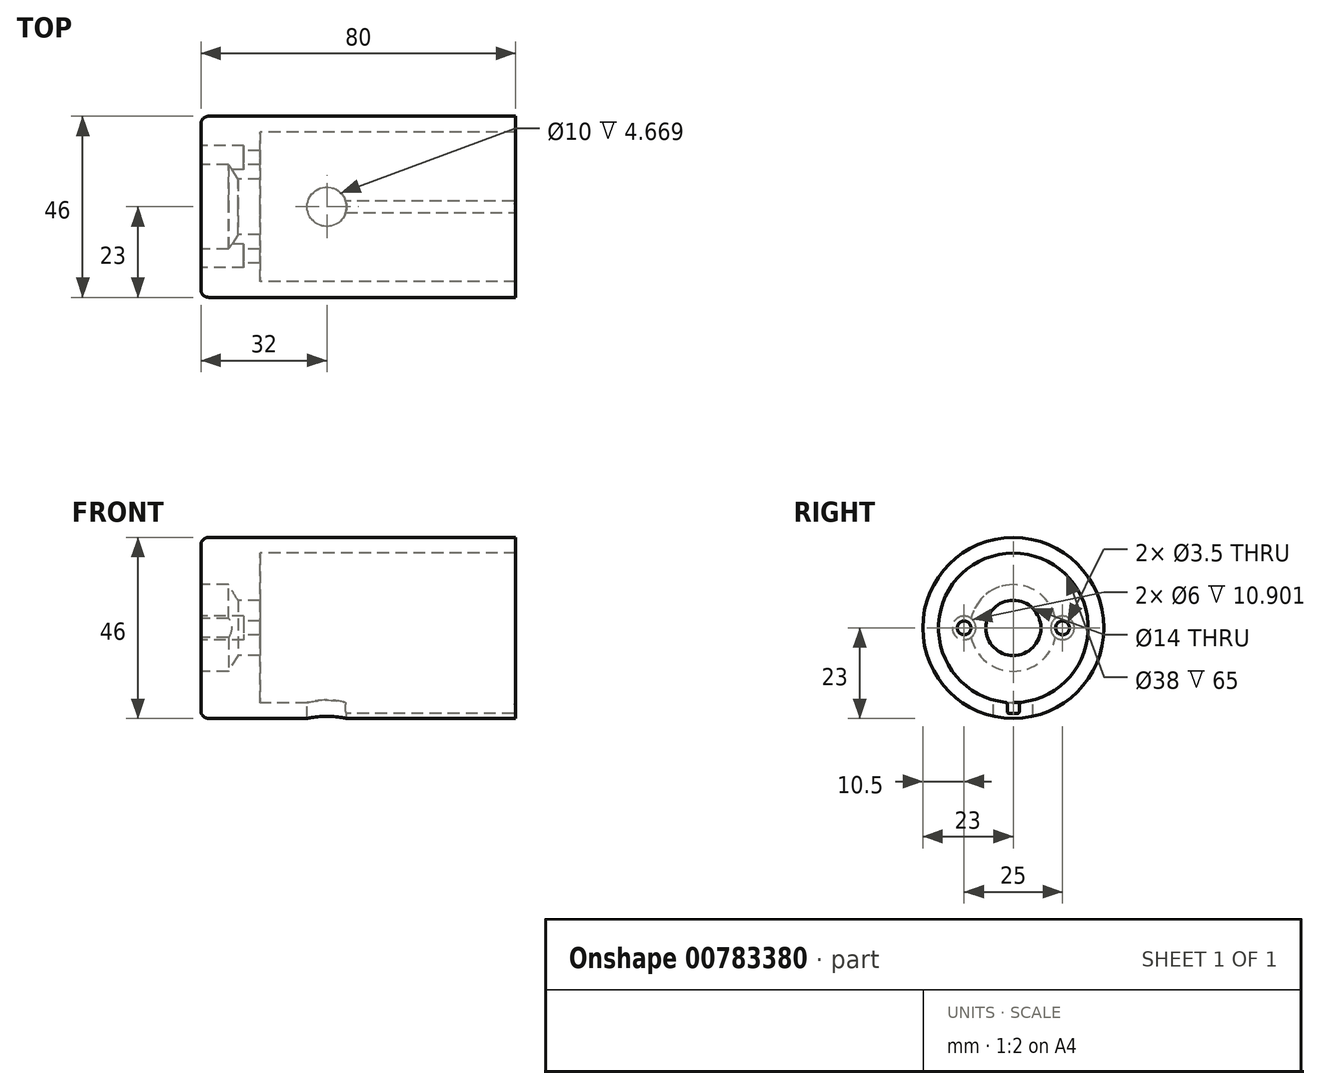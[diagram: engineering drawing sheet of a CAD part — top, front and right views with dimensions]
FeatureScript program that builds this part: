
annotation { "Feature Type Name" : "Feature", "Feature Type Description" : "" }
export const myFeature = defineFeature(function(context is Context, id is Id, definition is map)
    precondition{}
    {
        {
            var Q0;
            Q0=qCreatedBy(makeId("Right.planeOp"),FACE);
            var sketch = newSketch(context, id + "F0", { "sketchPlane" : qUnion([Q0])});
            skCircle(sketch, "E0", {"center": v(0, 0) * mm, "radius": 23 * mm});
            skCircle(sketch, "E1", {"center": v(0, 0) * mm, "radius": 19 * mm});
            skPoint(sketch, "E2", {"position": v(0, -23) * mm});
            skLineSegment(sketch, "E3", {"start": v(0, -23) * mm, "end": v(0, -18.78) * mm});
            skLineSegment(sketch, "E4", {"start": v(0, -18.78) * mm, "end": v(1.5, -18.78) * mm});
            skLineSegment(sketch, "E5", {"start": v(1.5, -18.78) * mm, "end": v(1.5, -21.78) * mm});
            skLineSegment(sketch, "E6", {"start": v(1.5, -21.78) * mm, "end": v(-1.5, -21.78) * mm});
            skLineSegment(sketch, "E7", {"start": v(-1.5, -21.78) * mm, "end": v(-1.5, -18.78) * mm});
            skLineSegment(sketch, "E8", {"start": v(-1.5, -18.78) * mm, "end": v(0, -18.78) * mm});
            skLineSegment(sketch, "E9", {"start": v(0, 0) * mm, "end": v(12.5, 0) * mm});
            skLineSegment(sketch, "E10", {"start": v(0, 0) * mm, "end": v(-12.5, 0) * mm});
            skSolve(sketch);
        }
        {
            var Q0;
            Q0=makeQuery(id+"F0.imprint","IMPRINT",FACE,{"disambiguationData":[TD([[makeQuery(id+"F0.imprint","IMPRINT",EDGE,{"derivedFrom":sQuery(id+"F0.wireOp",EDGE,"E0")}),1.0]])]});
            extrude(context, id + "F1", {"entities" : qUnion([Q0]), "depth" : 80 * mm, "offsetDistance" : 25 * mm});
        }
        {
            var Q0;
            Q0 = qSketchRegion(id + "F0", true);
            var Q1;
            {var subQ1=sQuery(id+"F0.wireOp",EDGE,"E4");Q1=makeQuery(id+"F0.imprint","IMPRINT",FACE,{"disambiguationData":[TD([[makeQuery(id+"F0.imprint","IMPRINT",EDGE,{"derivedFrom":subQ1}),1.0]])]});}
            var Q2;
            {var subQ0=sQuery(id+"F0.wireOp",EDGE,"E3");Q2=makeQuery(id+"F0.imprint","IMPRINT",FACE,{"disambiguationData":[TD([[makeQuery(id+"F0.imprint","IMPRINT",EDGE,{"derivedFrom":subQ0}),1.0]])]});}
            var Q3;
            {var subQ0=sQuery(id+"F0.wireOp",EDGE,"E3");Q3=makeQuery(id+"F0.imprint","IMPRINT",FACE,{"disambiguationData":[TD([[makeQuery(id+"F0.imprint","IMPRINT",EDGE,{"derivedFrom":subQ0}),-1.0]])]});}
            extrude(context, id + "F2", {"entities" : qUnion([Q0, Q1, Q2, Q3]), "operationType" : NewBodyOperationType.ADD, "depth" : 15 * mm, "offsetDistance" : 25 * mm});
        }
        {
            var Q0;
            Q0=qCreatedBy(makeId("Top.planeOp"),FACE);
            var sketch = newSketch(context, id + "F3", { "sketchPlane" : qUnion([Q0])});
            skLineSegment(sketch, "E11", {"start": v(0, 0) * mm, "end": v(32, 0) * mm});
            skSolve(sketch);
        }
        {
            var Q0;
            {var subQ0=sQuery(id+"F0.wireOp",EDGE,"E6");Q0=makeQuery(id+"F0.imprint","IMPRINT",FACE,{"disambiguationData":[TD([[makeQuery(id+"F0.imprint","IMPRINT",EDGE,{"derivedFrom":subQ0}),-1.0]])]});}
            extrude(context, id + "F4", {"entities" : qUnion([Q0]), "operationType" : NewBodyOperationType.ADD, "depth" : 28 * mm, "offsetDistance" : 25 * mm});
        }
        {
            var Q0;
            Q0=sQuery(id+"F3.wireOp",VERTEX,"E11.end");
            var Q1;
            Q1=makeQuery(id+"F1.opExtrude","SWEPT_BODY",BODY,{"disambiguationData":[OSD([sQuery(id+"F0.wireOp",EDGE,"E0"),sQuery(id+"F0.wireOp",EDGE,"E1"),sQuery(id+"F0.wireOp",EDGE,"E5"),sQuery(id+"F0.wireOp",EDGE,"E6"),sQuery(id+"F0.wireOp",EDGE,"E7")])]});
            hole(context, id + "F5", {"style" : HoleStyle.SIMPLE, "endStyle" : HoleEndStyle.THROUGH, "holeDiameter" : 10 * mm, "majorDiameter" : 5 * mm, "isTappedThrough" : true, "tappedDepth" : 12 * mm, "tapClearance" : 3, "locations" : qUnion([Q0]), "scope" : qUnion([Q1])});
        }
        {
            var Q0;
            Q0=sQuery(id+"F0.wireOp",VERTEX,"E0.center");
            var Q1;
            Q1=makeQuery(id+"F1.opExtrude","SWEPT_BODY",BODY,{"disambiguationData":[OSD([sQuery(id+"F0.wireOp",EDGE,"E0"),sQuery(id+"F0.wireOp",EDGE,"E1"),sQuery(id+"F0.wireOp",EDGE,"E5"),sQuery(id+"F0.wireOp",EDGE,"E6"),sQuery(id+"F0.wireOp",EDGE,"E7")])]});
            hole(context, id + "F6", {"style" : HoleStyle.SIMPLE, "endStyle" : HoleEndStyle.THROUGH, "oppositeDirection" : true, "holeDiameter" : 14 * mm, "majorDiameter" : 5 * mm, "isTappedThrough" : true, "tappedDepth" : 12 * mm, "tapClearance" : 3, "locations" : qUnion([Q0]), "scope" : qUnion([Q1])});
        }
        {
            var Q0;
            Q0=sQuery(id+"F0.wireOp",VERTEX,"E0.center");
            var Q1;
            Q1=makeQuery(id+"F1.opExtrude","SWEPT_BODY",BODY,{"disambiguationData":[OSD([sQuery(id+"F0.wireOp",EDGE,"E0"),sQuery(id+"F0.wireOp",EDGE,"E1"),sQuery(id+"F0.wireOp",EDGE,"E5"),sQuery(id+"F0.wireOp",EDGE,"E6"),sQuery(id+"F0.wireOp",EDGE,"E7")])]});
            hole(context, id + "F7", {"style" : HoleStyle.SIMPLE, "endStyle" : HoleEndStyle.BLIND, "oppositeDirection" : true, "holeDiameter" : 22 * mm, "majorDiameter" : 5 * mm, "holeDepth" : 7 * mm, "isTappedThrough" : true, "tappedDepth" : 12 * mm, "tapClearance" : 3, "locations" : qUnion([Q0]), "scope" : qUnion([Q1])});
        }
        {
            var Q0;
            Q0=sQuery(id+"F0.wireOp",VERTEX,"E9.end");
            var Q1;
            Q1=sQuery(id+"F0.wireOp",VERTEX,"E10.end");
            var Q2;
            Q2=makeQuery(id+"F1.opExtrude","SWEPT_BODY",BODY,{"disambiguationData":[OSD([sQuery(id+"F0.wireOp",EDGE,"E0"),sQuery(id+"F0.wireOp",EDGE,"E1"),sQuery(id+"F0.wireOp",EDGE,"E5"),sQuery(id+"F0.wireOp",EDGE,"E6"),sQuery(id+"F0.wireOp",EDGE,"E7")])]});
            hole(context, id + "F8", {"style" : HoleStyle.C_BORE, "endStyle" : HoleEndStyle.THROUGH, "oppositeDirection" : true, "holeDiameter" : 3.5 * mm, "cBoreDiameter" : 6 * mm, "cBoreDepth" : 3 * mm, "majorDiameter" : 5 * mm, "isTappedThrough" : true, "tappedDepth" : 12 * mm, "tapClearance" : 3, "locations" : qUnion([Q0, Q1]), "scope" : qUnion([Q2])});
        }
        {
            var Q0;
            Q0=makeQuery(id+"F2.boolean.opBoolean","SPLIT",EDGE,{"derivedFrom":makeQuery(id+"F1.opExtrude","SWEPT_EDGE",EDGE,{"disambiguationData":[OSD([sQuery(id+"F0.wireOp",EDGE,"E0"),sQuery(id+"F0.wireOp",EDGE,"E5")])]})});
            var Q1;
            Q1=makeQuery(id+"F2.boolean.opBoolean","SPLIT",EDGE,{"derivedFrom":makeQuery(id+"F1.opExtrude","SWEPT_EDGE",EDGE,{"disambiguationData":[OSD([sQuery(id+"F0.wireOp",EDGE,"E0"),sQuery(id+"F0.wireOp",EDGE,"E7")])]})});
            var Q2;
            Q2=makeQuery(id+"F1.opExtrude","CAP_EDGE",EDGE,{"disambiguationData":[OSD([sQuery(id+"F0.wireOp",EDGE,"E5")])],"isStart":false});
            var Q3;
            Q3=makeQuery(id+"F1.opExtrude","CAP_EDGE",EDGE,{"disambiguationData":[OSD([sQuery(id+"F0.wireOp",EDGE,"E7")])],"isStart":false});
            var Q4;
            Q4=makeQuery(id+"F7.hole-0.boolean.opBoolean","COPY",EDGE,{"derivedFrom":makeQuery(id+"F7.hole-0.opRevolve","SWEPT_EDGE",EDGE,{"disambiguationData":[OSD([sQuery(id+"F7.hole-0.sketch.wireOp",EDGE,"core_line_2"),sQuery(id+"F7.hole-0.sketch.wireOp",EDGE,"core_line_3")])]})});
            var Q5;
            Q5=makeQuery(id+"F7.hole-0.boolean.opBoolean","INTERSECT",EDGE,{"derivedFrom":[makeQuery(id+"F6.hole-0.boolean.opBoolean","COPY",FACE,{"derivedFrom":makeQuery(id+"F6.hole-0.opRevolve","SWEPT_FACE",FACE,{"disambiguationData":[OSD([sQuery(id+"F6.hole-0.sketch.wireOp",EDGE,"core_line_2")])]})}),makeQuery(id+"F7.hole-0.opRevolve","SWEPT_FACE",FACE,{"disambiguationData":[OSD([sQuery(id+"F7.hole-0.sketch.wireOp",EDGE,"core_line_1")])]})]});
            var Q6;
            Q6=makeQuery(id+"F6.hole-0.boolean.opBoolean","INTERSECT",EDGE,{"derivedFrom":[makeQuery(id+"F2.opExtrude","CAP_FACE",FACE,{"disambiguationData":[OSD([sQuery(id+"F0.wireOp",EDGE,"E0"),sQuery(id+"F0.wireOp",EDGE,"E1"),sQuery(id+"F0.wireOp",EDGE,"E5"),sQuery(id+"F0.wireOp",EDGE,"E6"),sQuery(id+"F0.wireOp",EDGE,"E7")])],"isStart":false}),makeQuery(id+"F6.hole-0.opRevolve","SWEPT_FACE",FACE,{"disambiguationData":[OSD([sQuery(id+"F6.hole-0.sketch.wireOp",EDGE,"core_line_2")])]})]});
            var Q7;
            Q7=makeQuery(id+"F8.hole-0.boolean.opBoolean","COPY",EDGE,{"derivedFrom":makeQuery(id+"F8.hole-0.opRevolve","SWEPT_EDGE",EDGE,{"disambiguationData":[OSD([sQuery(id+"F8.hole-0.sketch.wireOp",EDGE,"cbore_start_line_2"),sQuery(id+"F8.hole-0.sketch.wireOp",EDGE,"cbore_start_line_3")])]})});
            var Q8;
            Q8=makeQuery(id+"F8.hole-1.boolean.opBoolean","COPY",EDGE,{"derivedFrom":makeQuery(id+"F8.hole-1.opRevolve","SWEPT_EDGE",EDGE,{"disambiguationData":[OSD([sQuery(id+"F8.hole-1.sketch.wireOp",EDGE,"cbore_start_line_2"),sQuery(id+"F8.hole-1.sketch.wireOp",EDGE,"cbore_start_line_3")])]})});
            var Q9;
            Q9=makeQuery(id+"F8.hole-0.boolean.opBoolean","INTERSECT",EDGE,{"disambiguationData":[OD(1.0)],"derivedFrom":[makeQuery(id+"F7.hole-0.boolean.opBoolean","COPY",FACE,{"derivedFrom":makeQuery(id+"F7.hole-0.opRevolve","SWEPT_FACE",FACE,{"disambiguationData":[OSD([sQuery(id+"F7.hole-0.sketch.wireOp",EDGE,"core_line_2")])]})}),makeQuery(id+"F8.hole-0.opRevolve","SWEPT_FACE",FACE,{"disambiguationData":[OSD([sQuery(id+"F8.hole-0.sketch.wireOp",EDGE,"cbore_start_line_2")])]})]});
            var Q10;
            Q10=makeQuery(id+"F8.hole-0.boolean.opBoolean","INTERSECT",EDGE,{"disambiguationData":[OD(0.0)],"derivedFrom":[makeQuery(id+"F7.hole-0.boolean.opBoolean","COPY",FACE,{"derivedFrom":makeQuery(id+"F7.hole-0.opRevolve","SWEPT_FACE",FACE,{"disambiguationData":[OSD([sQuery(id+"F7.hole-0.sketch.wireOp",EDGE,"core_line_2")])]})}),makeQuery(id+"F8.hole-0.opRevolve","SWEPT_FACE",FACE,{"disambiguationData":[OSD([sQuery(id+"F8.hole-0.sketch.wireOp",EDGE,"cbore_start_line_2")])]})]});
            var Q11;
            Q11=makeQuery(id+"F8.hole-1.boolean.opBoolean","INTERSECT",EDGE,{"disambiguationData":[OD(1.0)],"derivedFrom":[makeQuery(id+"F7.hole-0.boolean.opBoolean","COPY",FACE,{"derivedFrom":makeQuery(id+"F7.hole-0.opRevolve","SWEPT_FACE",FACE,{"disambiguationData":[OSD([sQuery(id+"F7.hole-0.sketch.wireOp",EDGE,"core_line_2")])]})}),makeQuery(id+"F8.hole-1.opRevolve","SWEPT_FACE",FACE,{"disambiguationData":[OSD([sQuery(id+"F8.hole-1.sketch.wireOp",EDGE,"cbore_start_line_2")])]})]});
            var Q12;
            Q12=makeQuery(id+"F8.hole-1.boolean.opBoolean","INTERSECT",EDGE,{"disambiguationData":[OD(0.0)],"derivedFrom":[makeQuery(id+"F7.hole-0.boolean.opBoolean","COPY",FACE,{"derivedFrom":makeQuery(id+"F7.hole-0.opRevolve","SWEPT_FACE",FACE,{"disambiguationData":[OSD([sQuery(id+"F7.hole-0.sketch.wireOp",EDGE,"core_line_2")])]})}),makeQuery(id+"F8.hole-1.opRevolve","SWEPT_FACE",FACE,{"disambiguationData":[OSD([sQuery(id+"F8.hole-1.sketch.wireOp",EDGE,"cbore_start_line_2")])]})]});
            var Q13;
            Q13=makeQuery(id+"F8.hole-0.boolean.opBoolean","INTERSECT",EDGE,{"derivedFrom":[makeQuery(id+"F7.hole-0.boolean.opBoolean","COPY",FACE,{"derivedFrom":makeQuery(id+"F7.hole-0.opRevolve","SWEPT_FACE",FACE,{"disambiguationData":[OSD([sQuery(id+"F7.hole-0.sketch.wireOp",EDGE,"core_line_1")])]})}),makeQuery(id+"F8.hole-0.opRevolve","SWEPT_FACE",FACE,{"disambiguationData":[OSD([sQuery(id+"F8.hole-0.sketch.wireOp",EDGE,"cbore_start_line_2")])]})]});
            var Q14;
            Q14=makeQuery(id+"F8.hole-1.boolean.opBoolean","INTERSECT",EDGE,{"derivedFrom":[makeQuery(id+"F7.hole-0.boolean.opBoolean","COPY",FACE,{"derivedFrom":makeQuery(id+"F7.hole-0.opRevolve","SWEPT_FACE",FACE,{"disambiguationData":[OSD([sQuery(id+"F7.hole-0.sketch.wireOp",EDGE,"core_line_1")])]})}),makeQuery(id+"F8.hole-1.opRevolve","SWEPT_FACE",FACE,{"disambiguationData":[OSD([sQuery(id+"F8.hole-1.sketch.wireOp",EDGE,"cbore_start_line_2")])]})]});
            var Q15;
            Q15=makeQuery(id+"F8.hole-1.boolean.opBoolean","COPY",EDGE,{"derivedFrom":makeQuery(id+"F8.hole-1.opRevolve","SWEPT_EDGE",EDGE,{"disambiguationData":[OSD([sQuery(id+"F8.hole-1.sketch.wireOp",EDGE,"cbore_start_line_1"),sQuery(id+"F8.hole-1.sketch.wireOp",EDGE,"core_line_2")])]})});
            var Q16;
            Q16=makeQuery(id+"F8.hole-0.boolean.opBoolean","COPY",EDGE,{"derivedFrom":makeQuery(id+"F8.hole-0.opRevolve","SWEPT_EDGE",EDGE,{"disambiguationData":[OSD([sQuery(id+"F8.hole-0.sketch.wireOp",EDGE,"cbore_start_line_1"),sQuery(id+"F8.hole-0.sketch.wireOp",EDGE,"core_line_2")])]})});
            var Q17;
            Q17=makeQuery(id+"F8.hole-1.boolean.opBoolean","INTERSECT",EDGE,{"derivedFrom":[makeQuery(id+"F2.opExtrude","CAP_FACE",FACE,{"disambiguationData":[OSD([sQuery(id+"F0.wireOp",EDGE,"E0")])],"isStart":false}),makeQuery(id+"F8.hole-1.opRevolve","SWEPT_FACE",FACE,{"disambiguationData":[OSD([sQuery(id+"F8.hole-1.sketch.wireOp",EDGE,"core_line_2")])]})]});
            var Q18;
            Q18=makeQuery(id+"F8.hole-0.boolean.opBoolean","INTERSECT",EDGE,{"derivedFrom":[makeQuery(id+"F2.opExtrude","CAP_FACE",FACE,{"disambiguationData":[OSD([sQuery(id+"F0.wireOp",EDGE,"E0")])],"isStart":false}),makeQuery(id+"F8.hole-0.opRevolve","SWEPT_FACE",FACE,{"disambiguationData":[OSD([sQuery(id+"F8.hole-0.sketch.wireOp",EDGE,"core_line_2")])]})]});
            fillet(context, id + "F9", {"entities" : qUnion([Q0, Q1, Q2, Q3, Q4, Q5, Q6, Q7, Q8, Q9, Q10, Q11, Q12, Q13, Q14, Q15, Q16, Q17, Q18]), "radius" : 0.5 * mm, "tangentPropagation" : true, "allowEdgeOverflow" : false});
        }
        {
            var Q0;
            Q0=makeQuery(id+"F1.opExtrude","CAP_EDGE",EDGE,{"disambiguationData":[OSD([sQuery(id+"F0.wireOp",EDGE,"E1")])],"isStart":true});
            var Q1;
            Q1=makeQuery(id+"F1.opExtrude","CAP_EDGE",EDGE,{"disambiguationData":[OSD([sQuery(id+"F0.wireOp",EDGE,"E0")])],"isStart":true});
            fillet(context, id + "F10", {"entities" : qUnion([Q0, Q1]), "radius" : 2 * mm, "tangentPropagation" : true, "allowEdgeOverflow" : false});
        }
    });
